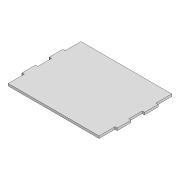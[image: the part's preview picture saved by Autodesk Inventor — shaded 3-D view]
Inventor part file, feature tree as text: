
AUTODESK INVENTOR PART (.ipt)
format: ipt  version: 2022 (Build 260153000, 153)  size: 99,328 bytes
history: native  units: mm
features: extrude x1, sketch x1
ambient origin geometry x8: Origin, YZ Plane, XZ Plane, XY Plane, X Axis, Y Axis, Z Axis, Center Point
bodies: Solid1 (feature_tree)
feature tree (2):
  extrude  "Extrusion1"  Depth=160.0mm
  sketch  "Sketch1"  dims[d0=200.0mm d1=160.0mm d2=5.0mm d3=30.0mm d4=5.0mm d5=30.0mm d6=30.0mm d7=15.0mm d8=5.0mm d9=0.0mm]
